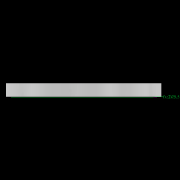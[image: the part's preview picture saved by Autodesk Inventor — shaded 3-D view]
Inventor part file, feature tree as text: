
AUTODESK INVENTOR PART (.ipt)
format: ipt  version: 2022.2 (Build 262287010, 287A)  size: 908,288 bytes
history: native  units: mm
features: extrude x20, sketch x19, pattern_circular x15, other x14, revolve x7, hole x7, move_body x4, fillet x2, draft x2
ambient origin geometry x8: Origin, YZ Plane, XZ Plane, XY Plane, X Axis, Y Axis, Z Axis, Center Point
bodies: Solid1 (feature_tree), Solid2 (feature_tree), Solid3 (feature_tree), Solid4 (feature_tree), Solid5 (feature_tree)
feature tree (90):
  sketch  "Sketch7"  dims[d21=0.5mm]
  other  "Roller1"
  other  "Roller2"
  sketch  "Sketch22"  dims[d39=0.05mm]
  sketch  "Sketch2"  dims[d17=0.05mm]
  sketch  "Sketch23"  dims[d41=0.05mm]
  other  "RevRoller1"
  fillet  "Fillet1"  Radius=0.05mm
  pattern_circular  "Circular Pattern13"  Count=6  [1 undecoded]
  move_body  "Move Body7"
  revolve  "Revolution13"  Angle=30.0deg
  fillet  "Fillet3"  [1 undecoded]
  pattern_circular  "Circular Pattern14"  [2 undecoded]
  move_body  "Move Body6"
  revolve  "Revolution14"  Angle=90.0deg
  extrude  "Extrusion23"  Depth=5.251mm
  other  "OuterRim_Top2"
  other  "OuterRim_Bottom2"
  extrude  "Extrusion9"  Depth=5.251mm
  sketch  "Sketch24"  dims[d42=0.5mm]
  extrude  "Extrusion10"  Depth=5.251mm
  extrude  "Extrusion11"  Depth=5.251mm
  pattern_circular  "Circular Pattern15"  [2 undecoded]
  sketch  "Sketch25"  dims[d43=0.5mm]
  extrude  "Extrusion12"  Depth=5.251mm
  extrude  "Extrusion14"  Depth=5.251mm
  extrude  "Extrusion15"  Depth=5.251mm
  pattern_circular  "Circular Pattern16"  [2 undecoded]
  extrude  "Extrusion16"  Depth=5.251mm
  extrude  "Extrusion17"  Depth=5.251mm
  hole  "Hole9"  [1 undecoded]
  pattern_circular  "Circular Pattern17"  [2 undecoded]
  sketch  "Sketch27"  dims[d45=0.5mm]
  hole  "Hole10"  [1 undecoded]
  hole  "Hole11"  [1 undecoded]
  pattern_circular  "Circular Pattern18"  [2 undecoded]
  extrude  "Extrusion18"  Depth=5.251mm
  extrude  "Extrusion19"  Depth=5.251mm
  pattern_circular  "Circular Pattern19"  [2 undecoded]
  sketch  "Sketch28"  dims[d46=0.5mm]
  extrude  "Extrusion20"  Depth=5.251mm
  extrude  "Extrusion22"  Depth=5.251mm
  pattern_circular  "Circular Pattern21"  [2 undecoded]
  draft  "FaceDraft2"
  other  "InnerRim"
  other  "OuterRim_Top"
  other  "OuterRim_Bottom"
  extrude  "Extrusion2"  TaperAngle=90.0deg  [1 undecoded]
  sketch  "Sketch13"  dims[d24=0.5mm]
  extrude  "Extrusion3"  TaperAngle=30.0deg  [1 undecoded]
  sketch  "Sketch15"  dims[d29=360.0deg d30=60.0mm]
  extrude  "Extrusion4"  TaperAngle=90.0deg  [1 undecoded]
  extrude  "Extrusion5"  Depth=5.251mm
  pattern_circular  "Circular Pattern6"  [2 undecoded]
  sketch  "Sketch16"  dims[d31=360.0deg d35=30.0deg d36=90.0deg]
  extrude  "Extrusion6"  Depth=55.5mm
  extrude  "Extrusion7"  TaperAngle=90.0deg  [1 undecoded]
  pattern_circular  "Circular Pattern7"  Angle=90.0deg  [1 undecoded]
  hole  "Hole5"  [1 undecoded]
  pattern_circular  "Circular Pattern9"  [2 undecoded]
  draft  "FaceDraft1"
  hole  "Hole6"  [1 undecoded]
  pattern_circular  "Circular Pattern10"  Count=360  [1 undecoded]
  hole  "Hole7"  [1 undecoded]
  pattern_circular  "Circular Pattern11"  [2 undecoded]
  hole  "Hole8"  [1 undecoded]
  extrude  "Extrusion8"  TaperAngle=0.0deg  [1 undecoded]
  pattern_circular  "Circular Pattern12"  [2 undecoded]
  sketch  "Sketch8"  dims[d22=0.5mm]
  sketch  "Sketch9"  dims[d23=0.5mm]
  revolve  "Revolution4"  [1 undecoded]
  move_body  "Move Body4"
  revolve  "Revolution5"  [1 undecoded]
  sketch  "Sketch5"  dims[d19=0.5mm]
  sketch  "Sketch6"  dims[d20=0.5mm]
  revolve  "Revolution3"  [1 undecoded]
  sketch  "Sketch4"  dims[d18=0.05mm]
  revolve  "Revolution1"  [1 undecoded]
  pattern_circular  "Circular Pattern1"  Count=9  [1 undecoded]
  move_body  "Move Body3"
  revolve  "Revolution2"  Angle=360.0deg
  other  "2D Equation Curve1"
  sketch  "Sketch14"  dims[d28=2.0mm]
  other  "Work Axis1"
  other  "Work Axis2"
  other  "Work Axis3"
  other  "Work Axis4"
  other  "Work Axis5"
  sketch  "Sketch26"  dims[d44=0.5mm]
  sketch  "Sketch29"  dims[d47=0.5mm d48=2.0mm d50=90.0deg d56=14.029612mm d57=4.025mm d90=16.473921mm d107=0.05mm d108=0.05mm d109=0.05mm d110=0.05mm d112=0.5mm d113=0.5mm d114=0.5mm d115=14.644822mm d116=14.607374mm d117=1.0mm d118=0.05mm d119=0.05mm d120=0.05mm d121=0.05mm d122=0.5mm d123=0.5mm d124=14.644822mm d125=14.607374mm d126=1.0mm d127=90.0deg d128=30.0deg d129=90.0deg d167=8.972256mm d173=10.814812mm d201=55.5mm d202=90.0deg d203=90.0deg d204=90.0deg d218=55.5mm d226=5.4mm d232=0.0mm d233=3600.0mm d234=10.502mm d235=0.0mm d243=1.902mm d244=0.0mm d246=2.75mm d247=5.251mm d248=0.0mm d249=3.0mm d250=0.0mm d251=90.0mm d252=360.0deg d254=2.75mm d255=3.0mm d256=5.251mm d257=0.0mm d258=3.0mm d259=0.0mm d260=90.0mm d261=360.0deg d277=76.5mm d281=73.5mm d282=24.65mm d283=6.0mm d284=4.0mm d285=2.0mm d286=90.0deg d287=5.251mm d288=0.0mm d289=60.0mm d290=360.0deg d292=0.436332mm d293=60.0mm d294=90.0mm d295=3.0mm d296=6.0mm d297=5.5mm d298=3.0mm d299=90.0deg d300=5.251mm d301=0.0mm d302=60.0mm d303=360.0deg d305=30.0deg d306=73.5mm d307=24.65mm d308=6.0mm d309=5.5mm d310=3.0mm d311=90.0deg d312=5.251mm d313=0.0mm d314=60.0mm d315=360.0deg d317=90.0mm d318=60.0mm d319=30.0deg d320=5.4mm d321=5.4mm d322=3.0mm d323=6.0mm d324=5.5mm d325=3.0mm d326=90.0deg d327=5.251mm d328=0.0mm d329=2.4mm d330=0.0mm d331=60.0mm d332=360.0deg d343=17.307186mm d344=17.309884mm d345=0.025mm d346=0.025mm d347=0.1mm d348=0.1mm d349=17.309884mm d350=17.307186mm d351=0.025mm d352=0.025mm d354=0.1mm d355=17.307186mm d356=17.309884mm d357=1.0mm d358=90.0deg d359=0.5mm d360=60.0mm d361=360.0deg d363=30.0deg d367=8.1mm d369=4.014775mm d370=0.1mm d371=1.0mm d372=30.0deg d373=90.0deg d374=0.5mm d375=60.0mm d376=360.0deg d378=90.0deg d379=0.1mm d380=0.1mm d381=0.1mm d382=0.1mm d383=0.1mm d384=10.502mm d385=0.0mm d386=0.0mm d391=1.0mm d392=55.5mm d393=1.5mm d394=1.5mm d395=1.5mm d396=1.5mm d397=90.0deg d398=90.0deg d399=90.0deg d400=55.5mm d401=10.502mm d402=0.0mm d403=2.75mm d404=1.5mm d405=10.502mm d406=0.0mm d407=3.0mm d408=0.0mm d409=90.0mm d410=360.0deg d412=5.4mm d413=5.251mm d414=0.0mm d417=5.4mm d418=2.4mm d419=0.0mm d420=2.4mm d421=0.0mm d422=90.0mm d423=360.0deg d425=60.0mm d426=90.0mm d427=1.5mm d428=1.5mm d429=5.4mm d430=5.4mm d431=5.251mm d432=0.0mm d433=2.4mm d434=0.0mm d435=30.0deg d436=73.5mm d437=24.65mm d438=6.0mm d439=4.0mm d440=2.0mm d441=90.0deg d442=5.251mm d443=0.0mm d444=60.0mm d445=360.0deg d447=3.0mm d448=6.0mm d449=5.5mm d450=3.0mm d451=90.0deg d452=5.251mm d453=0.0mm d454=24.65mm d455=6.0mm d456=5.5mm d457=3.0mm d458=90.0deg d459=5.251mm d460=0.0mm d461=60.0mm d462=360.0deg d464=5.251mm d465=0.0mm d466=3.0mm d467=0.0mm d468=90.0mm d469=360.0deg d472=1.5mm d474=5.251mm d475=0.0mm d481=3.0mm d482=0.0mm d483=90.0mm d484=360.0deg d486=0.436332mm d487=0.0mm d488=15.0mm d489=0.0mm d490=0.0mm d491=2.0mm d49=0.872665mm d51=0.872665mm d52=0.872665mm d236=0.5mm d237=0.872665mm d238=0.5mm d239=0.872665mm d291=0.0625mm d415=0.5mm d416=0.872665mm d471=0.5mm d473=0.5mm]
note: 43 required parameter values undecoded (feature->parameter linkage not recoverable at this tier; creation-order binding heuristic only, values carry confidence <= 0.55)